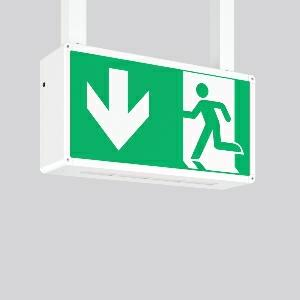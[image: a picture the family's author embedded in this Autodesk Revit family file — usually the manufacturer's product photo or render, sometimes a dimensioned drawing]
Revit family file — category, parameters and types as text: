
# Revit family: rechteck_rohrpendel_671089_002_04_08f4
name_source: partatom
category: Lighting Fixtures
units: mm (PartAtom-declared; Revit-internal decimal feet)

## family parameters
Cut with Voids When Loaded = No
Host = Face
Light Source = No
Part Type = Normal
Room Calculation Point = No
Round Connector Dimension = Use Diameter
Shared = No

## types (1)
- RECHTECK rohrpendel
    Apparent Load = 0 VA
    Default Elevation = 1800 mm
    Description = Series: RECHTECK
Rectangular pendant luminaire in classic design. For escape route identification. Housing: aluminium, with plastic corner connectors. Display panels: plastic, opal, with motifs on one side/on both sides. Aluminium pendant suspension. Electronic ballast included. Self-contained system with automatic self-test and feedback to the RZB monitoring system MULTIDIGIT. Please indicate legend number when placing your order! 
Colour: white
Length: 485 mm
Width: 125 mm
Height: 250 mm
Suspension length: 500 mm
Weight: 4.06 kg
Operating mode: maintained power mode
Viewing Distance: 43 m
Duration time: 3 h
Lamp: LED
Socket: without socket
Colour temperature: 6500K
Colour rendering index (CRI): 70
System power: 9.1 W
Control gear: Regulated power supply
Protection class: I
Type of protection: IP 44
    Height = 250 mm
    Lamp = 0 x
    Length = 485 mm
    Luminous efficacy = 0 lm/W
    Manufacturer = RZB
    ModVariant = No
    Model = 671089.002.04
    Mounting Place = Ceiling
    Mounting Type = Pendant
    Number of Poles = 1
    OnlyDefault = Yes
    Power Factor = 1
    Product Name = RECHTECK rohrpendel
    Product group = Pendant luminaires
    ProductGroupID = 902
    Protection Class = Protection class I
    Protection Degree = IP 44
    RLX_Detail_Level = 1
    RLX_Emergency_Light_Flux = 0 lm
    RLX_Emergency_Type = 0
    RLX_Emergency_Type_DB = No
    RlxData = <blob elided: 37537 chars, md5=971a42c7>
    Standby Power = 0 W
    System Light Flux = 0 lm
    System Power = 0 W
    Type Comments = Product without accessories
    Type Image = 671089.002.jpg
    URL = http://relux.com
    VarID = ---
    Voltage = 230 V
    Voltage Range = 220-240 V
    Weight = 0.00 kg
    Width = 125 mm

## geometry (parser evidence)
native form markers: Blend x4, Sweep x9
no freeform markers — native parametric forms only
